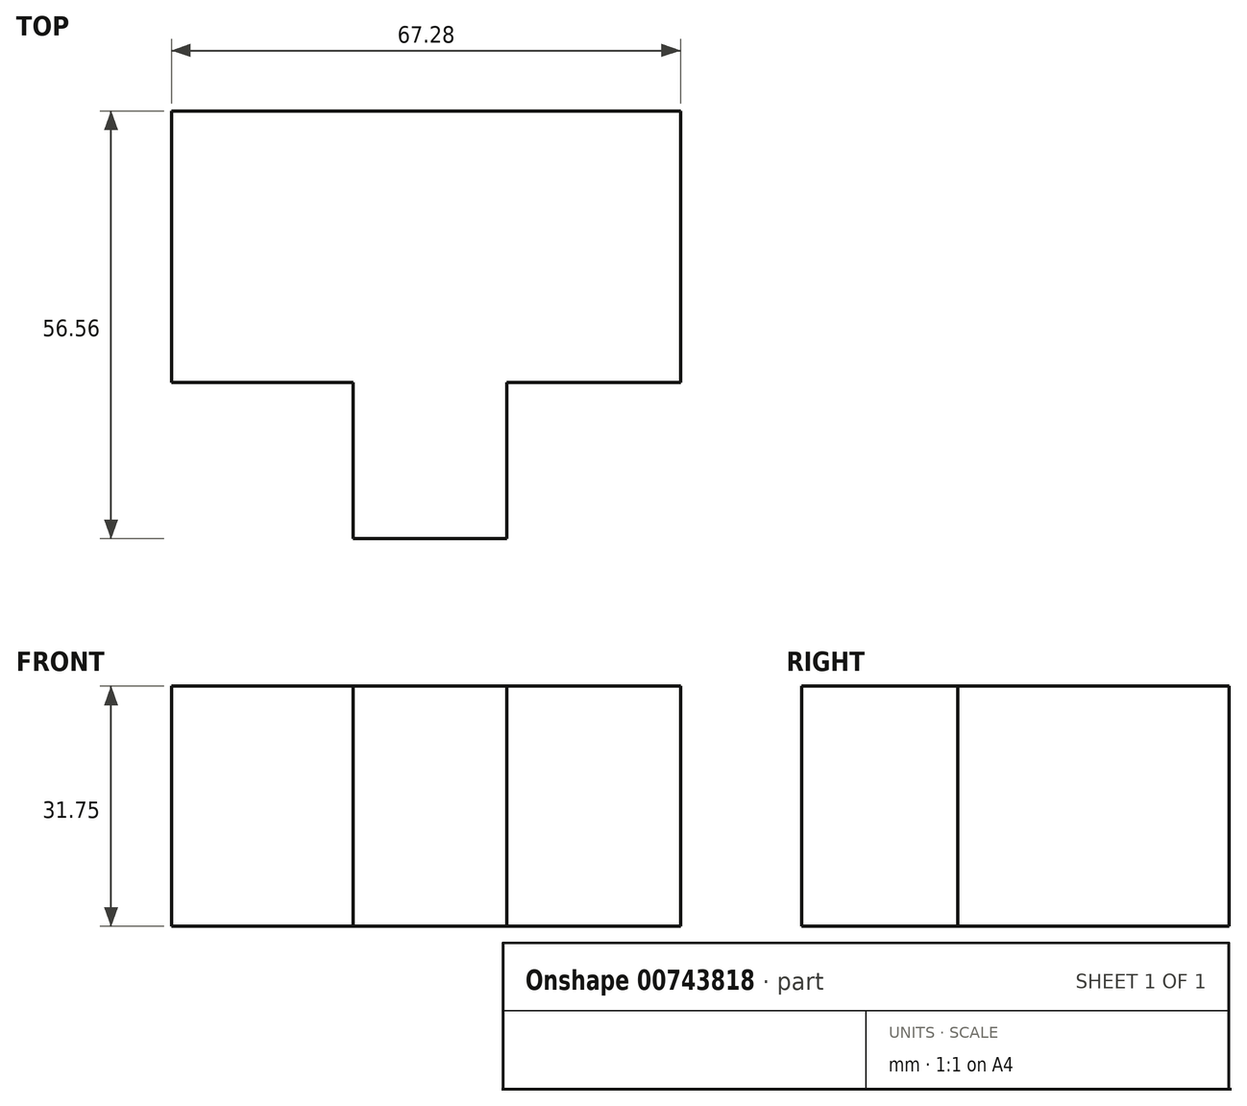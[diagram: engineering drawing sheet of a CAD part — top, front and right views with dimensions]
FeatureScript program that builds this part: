
annotation { "Feature Type Name" : "Feature", "Feature Type Description" : "" }
export const myFeature = defineFeature(function(context is Context, id is Id, definition is map)
    precondition{}
    {
        {
            var Q0;
            Q0=qCreatedBy(makeId("Top.planeOp"),FACE);
            var sketch = newSketch(context, id + "F0", { "sketchPlane" : qUnion([Q0])});
            skLineSegment(sketch, "E0", {"start": v(0, 0) * mm, "end": v(0, 16.52) * mm});
            skLineSegment(sketch, "E1", {"start": v(0, 16.52) * mm, "end": v(-19.2, 16.52) * mm});
            skLineSegment(sketch, "E2", {"start": v(-19.2, 16.52) * mm, "end": v(-19.2, 45.24) * mm});
            skLineSegment(sketch, "E3", {"start": v(-19.2, 45.24) * mm, "end": v(34.62, 45.24) * mm});
            skLineSegment(sketch, "E4", {"start": v(34.62, 45.24) * mm, "end": v(34.62, 16.52) * mm});
            skLineSegment(sketch, "E5", {"start": v(34.62, 16.52) * mm, "end": v(16.26, 16.52) * mm});
            skLineSegment(sketch, "E6", {"start": v(16.26, 16.52) * mm, "end": v(16.26, 0) * mm});
            skLineSegment(sketch, "E7", {"start": v(16.26, 0) * mm, "end": v(0, 0) * mm});
            skSolve(sketch);
        }
        {
            var Q0;
            Q0 = qSketchRegion(id + "F0", true);
            extrude(context, id + "F1", {"entities" : qUnion([Q0]), "depth" : 25.4 * mm, "offsetDistance" : 25.4 * mm});
        }
        {
            var Q0;
            Q0=makeQuery(id+"F1.opExtrude","SWEPT_BODY",BODY,{"disambiguationData":[OSD([sQuery(id+"F0.wireOp",EDGE,"E0"),sQuery(id+"F0.wireOp",EDGE,"E1"),sQuery(id+"F0.wireOp",EDGE,"E2"),sQuery(id+"F0.wireOp",EDGE,"E3"),sQuery(id+"F0.wireOp",EDGE,"E4"),sQuery(id+"F0.wireOp",EDGE,"E5"),sQuery(id+"F0.wireOp",EDGE,"E6"),sQuery(id+"F0.wireOp",EDGE,"E7")])]});
            var Q1;
            Q1=qCreatedBy(makeId("Origin.pointOp"),VERTEX);
            transform(context, id + "F2", {"entities" : qUnion([Q0]), "transformType" : TransformType.SCALE_UNIFORMLY, "scale" : 1.25, "scalePoint" : qUnion([Q1]), "makeCopy" : false});
        }
    });
